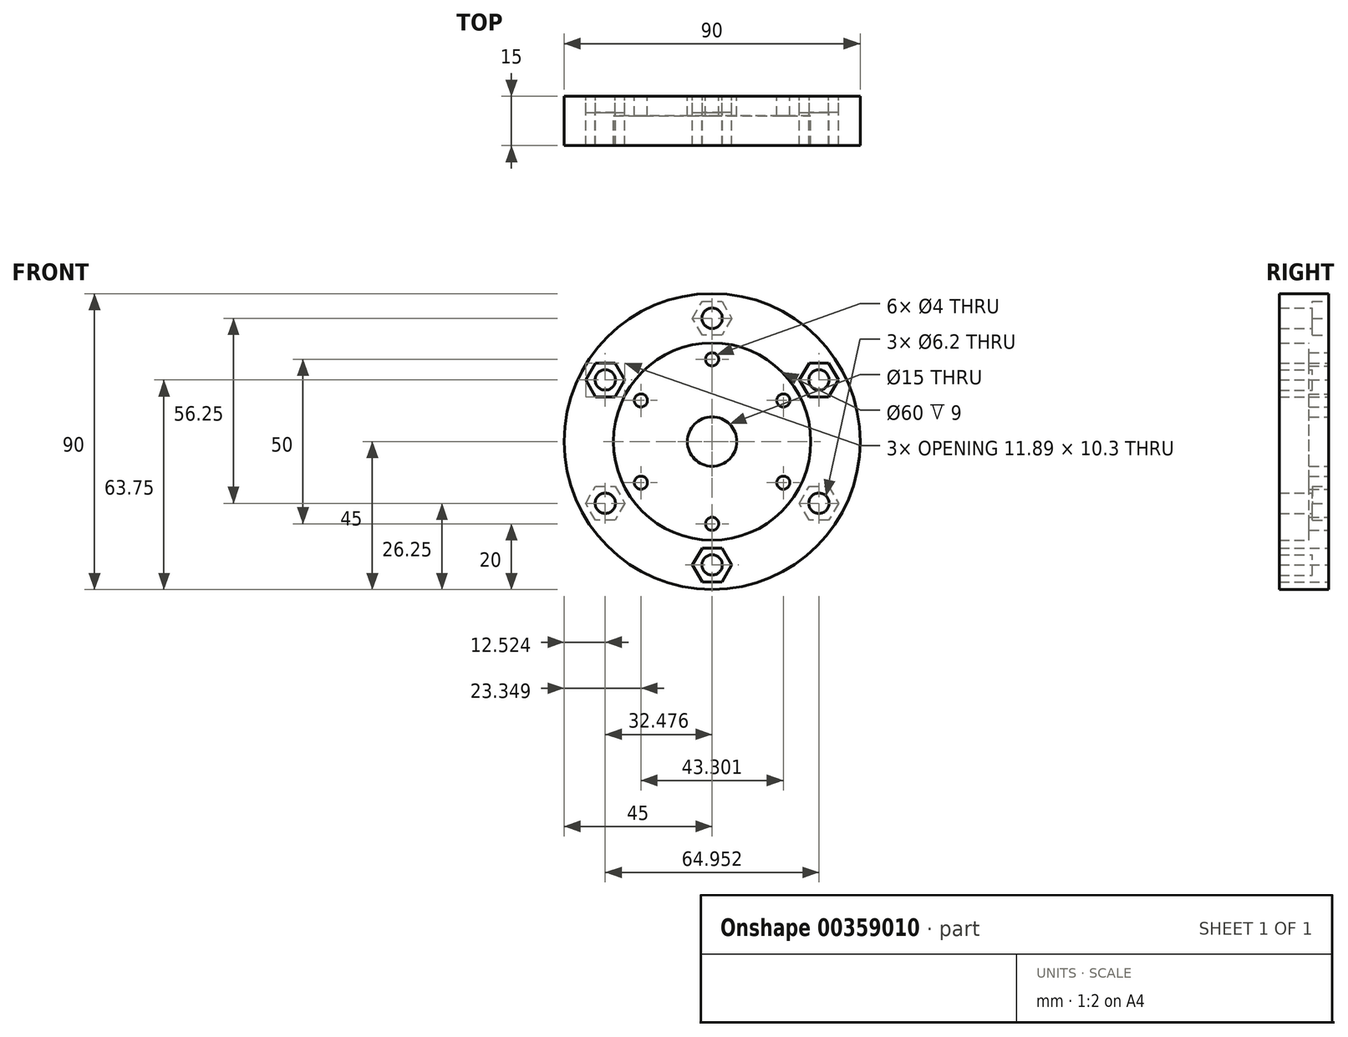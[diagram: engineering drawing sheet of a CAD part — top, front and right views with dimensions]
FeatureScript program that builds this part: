
annotation { "Feature Type Name" : "Feature", "Feature Type Description" : "" }
export const myFeature = defineFeature(function(context is Context, id is Id, definition is map)
    precondition{}
    {
        {
            var Q0;
            Q0=qCreatedBy(makeId("Front.planeOp"),FACE);
            var sketch = newSketch(context, id + "F0", { "sketchPlane" : qUnion([Q0])});
            skCircle(sketch, "E0", {"center": v(0, 0) * mm, "radius": 45 * mm});
            skCircle(sketch, "E1", {"center": v(0, 0) * mm, "radius": 7.5 * mm});
            skCircle(sketch, "E2", {"center": v(0, 25) * mm, "radius": 2 * mm});
            skCircle(sketch, "E3", {"center": v(0, 37.5) * mm, "radius": 3.1 * mm});
            skCircle(sketch, "E4.MirrorC", {"center": v(0, -25) * mm, "radius": 2 * mm});
            skCircle(sketch, "E5.MirrorC", {"center": v(0, -37.5) * mm, "radius": 3.1 * mm});
            skCircle(sketch, "E6.1.0", {"center": v(-32.48, -18.75) * mm, "radius": 3.1 * mm});
            skCircle(sketch, "E6.1.1", {"center": v(-21.65, -12.5) * mm, "radius": 2 * mm});
            skCircle(sketch, "E6.1.2", {"center": v(21.65, 12.5) * mm, "radius": 2 * mm});
            skCircle(sketch, "E6.1.3", {"center": v(32.48, 18.75) * mm, "radius": 3.1 * mm});
            skCircle(sketch, "E6.2.0", {"center": v(32.48, -18.75) * mm, "radius": 3.1 * mm});
            skCircle(sketch, "E6.2.1", {"center": v(21.65, -12.5) * mm, "radius": 2 * mm});
            skCircle(sketch, "E6.2.2", {"center": v(-21.65, 12.5) * mm, "radius": 2 * mm});
            skCircle(sketch, "E6.2.3", {"center": v(-32.48, 18.75) * mm, "radius": 3.1 * mm});
            skCircle(sketch, "E7", {"center": v(0, 0) * mm, "radius": 30 * mm});
            skPoint(sketch, "E8.0.midPoint", {"position": v(4.67, 35.32) * mm});
            skCircle(sketch, "E9.cCircle", {"center": v(0, 37.5) * mm, "radius": 5.15 * mm, "construction": true});
            skLineSegment(sketch, "E9.0", {"start": v(-2.97, 42.65) * mm, "end": v(2.97, 42.65) * mm});
            skLineSegment(sketch, "E9.1", {"start": v(2.97, 42.65) * mm, "end": v(5.95, 37.5) * mm});
            skLineSegment(sketch, "E9.2", {"start": v(5.95, 37.5) * mm, "end": v(2.97, 32.35) * mm});
            skLineSegment(sketch, "E9.3", {"start": v(2.97, 32.35) * mm, "end": v(-2.97, 32.35) * mm});
            skLineSegment(sketch, "E9.4", {"start": v(-2.97, 32.35) * mm, "end": v(-5.95, 37.5) * mm});
            skLineSegment(sketch, "E9.5", {"start": v(-5.95, 37.5) * mm, "end": v(-2.97, 42.65) * mm});
            skPoint(sketch, "E9.0.midPoint", {"position": v(0, 42.65) * mm});
            skCircle(sketch, "E10.MirrorC", {"center": v(0, -37.5) * mm, "radius": 5.15 * mm, "construction": true});
            skLineSegment(sketch, "E11.MirrorCS", {"start": v(-5.95, -37.5) * mm, "end": v(-2.97, -42.65) * mm});
            skLineSegment(sketch, "E12.MirrorCS", {"start": v(-2.97, -42.65) * mm, "end": v(2.97, -42.65) * mm});
            skLineSegment(sketch, "E13.MirrorCS", {"start": v(-2.97, -32.35) * mm, "end": v(-5.95, -37.5) * mm});
            skLineSegment(sketch, "E14.MirrorCS", {"start": v(2.97, -32.35) * mm, "end": v(-2.97, -32.35) * mm});
            skLineSegment(sketch, "E15.MirrorCS", {"start": v(5.95, -37.5) * mm, "end": v(2.97, -32.35) * mm});
            skLineSegment(sketch, "E16.MirrorCS", {"start": v(2.97, -42.65) * mm, "end": v(5.95, -37.5) * mm});
            skLineSegment(sketch, "E17.1.0", {"start": v(-26.53, 18.75) * mm, "end": v(-29.5, 13.6) * mm});
            skLineSegment(sketch, "E17.1.1", {"start": v(-29.5, 23.9) * mm, "end": v(-26.53, 18.75) * mm});
            skLineSegment(sketch, "E17.1.2", {"start": v(-35.45, 23.9) * mm, "end": v(-29.5, 23.9) * mm});
            skPoint(sketch, "E17.1.3", {"position": v(-36.94, 21.33) * mm});
            skLineSegment(sketch, "E17.1.4", {"start": v(-38.42, 18.75) * mm, "end": v(-35.45, 23.9) * mm});
            skLineSegment(sketch, "E17.1.5", {"start": v(-35.45, 13.6) * mm, "end": v(-38.42, 18.75) * mm});
            skLineSegment(sketch, "E17.1.6", {"start": v(-29.5, 13.6) * mm, "end": v(-35.45, 13.6) * mm});
            skLineSegment(sketch, "E17.2.0", {"start": v(-29.5, -13.6) * mm, "end": v(-26.53, -18.75) * mm});
            skLineSegment(sketch, "E17.2.1", {"start": v(-35.45, -13.6) * mm, "end": v(-29.5, -13.6) * mm});
            skLineSegment(sketch, "E17.2.2", {"start": v(-38.42, -18.75) * mm, "end": v(-35.45, -13.6) * mm});
            skPoint(sketch, "E17.2.3", {"position": v(-36.94, -21.32) * mm});
            skLineSegment(sketch, "E17.2.4", {"start": v(-35.45, -23.9) * mm, "end": v(-38.42, -18.75) * mm});
            skLineSegment(sketch, "E17.2.5", {"start": v(-29.5, -23.9) * mm, "end": v(-35.45, -23.9) * mm});
            skLineSegment(sketch, "E17.2.6", {"start": v(-26.53, -18.75) * mm, "end": v(-29.5, -23.9) * mm});
            skLineSegment(sketch, "E17.3.0", {"start": v(-2.97, -32.35) * mm, "end": v(2.97, -32.35) * mm});
            skLineSegment(sketch, "E17.3.1", {"start": v(-5.95, -37.5) * mm, "end": v(-2.97, -32.35) * mm});
            skLineSegment(sketch, "E17.3.2", {"start": v(-2.97, -42.65) * mm, "end": v(-5.95, -37.5) * mm});
            skPoint(sketch, "E17.3.3", {"position": v(0, -42.65) * mm});
            skLineSegment(sketch, "E17.3.4", {"start": v(2.97, -42.65) * mm, "end": v(-2.97, -42.65) * mm});
            skLineSegment(sketch, "E17.3.5", {"start": v(5.95, -37.5) * mm, "end": v(2.97, -42.65) * mm});
            skLineSegment(sketch, "E17.3.6", {"start": v(2.97, -32.35) * mm, "end": v(5.95, -37.5) * mm});
            skLineSegment(sketch, "E17.4.0", {"start": v(26.53, -18.75) * mm, "end": v(29.5, -13.6) * mm});
            skLineSegment(sketch, "E17.4.1", {"start": v(29.5, -23.9) * mm, "end": v(26.53, -18.75) * mm});
            skLineSegment(sketch, "E17.4.2", {"start": v(35.45, -23.9) * mm, "end": v(29.5, -23.9) * mm});
            skPoint(sketch, "E17.4.3", {"position": v(36.94, -21.33) * mm});
            skLineSegment(sketch, "E17.4.4", {"start": v(38.42, -18.75) * mm, "end": v(35.45, -23.9) * mm});
            skLineSegment(sketch, "E17.4.5", {"start": v(35.45, -13.6) * mm, "end": v(38.42, -18.75) * mm});
            skLineSegment(sketch, "E17.4.6", {"start": v(29.5, -13.6) * mm, "end": v(35.45, -13.6) * mm});
            skLineSegment(sketch, "E17.5.0", {"start": v(29.5, 13.6) * mm, "end": v(26.53, 18.75) * mm});
            skLineSegment(sketch, "E17.5.1", {"start": v(35.45, 13.6) * mm, "end": v(29.5, 13.6) * mm});
            skLineSegment(sketch, "E17.5.2", {"start": v(38.42, 18.75) * mm, "end": v(35.45, 13.6) * mm});
            skPoint(sketch, "E17.5.3", {"position": v(36.94, 21.32) * mm});
            skLineSegment(sketch, "E17.5.4", {"start": v(35.45, 23.9) * mm, "end": v(38.42, 18.75) * mm});
            skLineSegment(sketch, "E17.5.5", {"start": v(29.5, 23.9) * mm, "end": v(35.45, 23.9) * mm});
            skLineSegment(sketch, "E17.5.6", {"start": v(26.53, 18.75) * mm, "end": v(29.5, 23.9) * mm});
            skSolve(sketch);
        }
        {
            var Q0;
            Q0=makeQuery(id+"F0.imprint","IMPRINT",FACE,{"disambiguationData":[TD([[makeQuery(id+"F0.imprint","IMPRINT",EDGE,{"derivedFrom":sQuery(id+"F0.wireOp",EDGE,"E0")}),1.0]])]});
            var Q1;
            Q1=makeQuery(id+"F0.imprint","IMPRINT",FACE,{"disambiguationData":[TD([[makeQuery(id+"F0.imprint","IMPRINT",EDGE,{"derivedFrom":sQuery(id+"F0.wireOp",EDGE,"E6.1.3")}),1.0]])]});
            var Q2;
            Q2=makeQuery(id+"F0.imprint","IMPRINT",FACE,{"disambiguationData":[TD([[makeQuery(id+"F0.imprint","IMPRINT",EDGE,{"derivedFrom":sQuery(id+"F0.wireOp",EDGE,"E6.2.0")}),-1.0]])]});
            var Q3;
            Q3=makeQuery(id+"F0.imprint","IMPRINT",FACE,{"disambiguationData":[TD([[makeQuery(id+"F0.imprint","IMPRINT",EDGE,{"derivedFrom":sQuery(id+"F0.wireOp",EDGE,"E6.2.3")}),1.0]])]});
            var Q4;
            Q4=makeQuery(id+"F0.imprint","IMPRINT",FACE,{"disambiguationData":[TD([[makeQuery(id+"F0.imprint","IMPRINT",EDGE,{"derivedFrom":sQuery(id+"F0.wireOp",EDGE,"E3")}),-1.0]])]});
            var Q5;
            Q5=makeQuery(id+"F0.imprint","IMPRINT",FACE,{"disambiguationData":[TD([[makeQuery(id+"F0.imprint","IMPRINT",EDGE,{"derivedFrom":sQuery(id+"F0.wireOp",EDGE,"E6.1.0")}),-1.0]])]});
            var Q6;
            Q6=makeQuery(id+"F0.imprint","IMPRINT",FACE,{"disambiguationData":[TD([[makeQuery(id+"F0.imprint","IMPRINT",EDGE,{"derivedFrom":sQuery(id+"F0.wireOp",EDGE,"E5.MirrorC")}),1.0]])]});
            var Q7;
            Q7=makeQuery(id+"F0.imprint","IMPRINT",FACE,{"disambiguationData":[TD([[makeQuery(id+"F0.imprint","IMPRINT",EDGE,{"derivedFrom":sQuery(id+"F0.wireOp",EDGE,"E1")}),-1.0]])]});
            extrude(context, id + "F1", {"entities" : qUnion([Q0, Q1, Q2, Q3, Q4, Q5, Q6, Q7]), "depth" : 15 * mm});
        }
        {
            var Q0;
            Q0=makeQuery(id+"F0.imprint","IMPRINT",FACE,{"disambiguationData":[TD([[makeQuery(id+"F0.imprint","IMPRINT",EDGE,{"derivedFrom":sQuery(id+"F0.wireOp",EDGE,"E6.2.3")}),1.0]])]});
            var Q1;
            Q1=makeQuery(id+"F0.imprint","IMPRINT",FACE,{"disambiguationData":[TD([[makeQuery(id+"F0.imprint","IMPRINT",EDGE,{"derivedFrom":sQuery(id+"F0.wireOp",EDGE,"E3")}),-1.0]])]});
            var Q2;
            Q2=makeQuery(id+"F0.imprint","IMPRINT",FACE,{"disambiguationData":[TD([[makeQuery(id+"F0.imprint","IMPRINT",EDGE,{"derivedFrom":sQuery(id+"F0.wireOp",EDGE,"E6.1.3")}),1.0]])]});
            var Q3;
            Q3=makeQuery(id+"F0.imprint","IMPRINT",FACE,{"disambiguationData":[TD([[makeQuery(id+"F0.imprint","IMPRINT",EDGE,{"derivedFrom":sQuery(id+"F0.wireOp",EDGE,"E6.2.0")}),-1.0]])]});
            var Q4;
            Q4=makeQuery(id+"F0.imprint","IMPRINT",FACE,{"disambiguationData":[TD([[makeQuery(id+"F0.imprint","IMPRINT",EDGE,{"derivedFrom":sQuery(id+"F0.wireOp",EDGE,"E5.MirrorC")}),1.0]])]});
            var Q5;
            Q5=makeQuery(id+"F0.imprint","IMPRINT",FACE,{"disambiguationData":[TD([[makeQuery(id+"F0.imprint","IMPRINT",EDGE,{"derivedFrom":sQuery(id+"F0.wireOp",EDGE,"E6.1.0")}),-1.0]])]});
            extrude(context, id + "F2", {"entities" : qUnion([Q0, Q1, Q2, Q3, Q4, Q5]), "operationType" : NewBodyOperationType.REMOVE, "depth" : 5 * mm, "hasSecondDirection" : true, "secondDirectionOppositeDirection" : true, "secondDirectionDepth" : 0 * mm, "offsetDistance" : 25 * mm});
        }
        {
            var Q0;
            Q0=makeQuery(id+"F0.imprint","IMPRINT",FACE,{"disambiguationData":[TD([[makeQuery(id+"F0.imprint","IMPRINT",EDGE,{"derivedFrom":sQuery(id+"F0.wireOp",EDGE,"E1")}),-1.0]])]});
            extrude(context, id + "F3", {"entities" : qUnion([Q0]), "operationType" : NewBodyOperationType.REMOVE, "depth" : 15 * mm, "hasSecondDirection" : true, "secondDirectionOppositeDirection" : false, "secondDirectionDepth" : 6 * mm});
        }
    });
